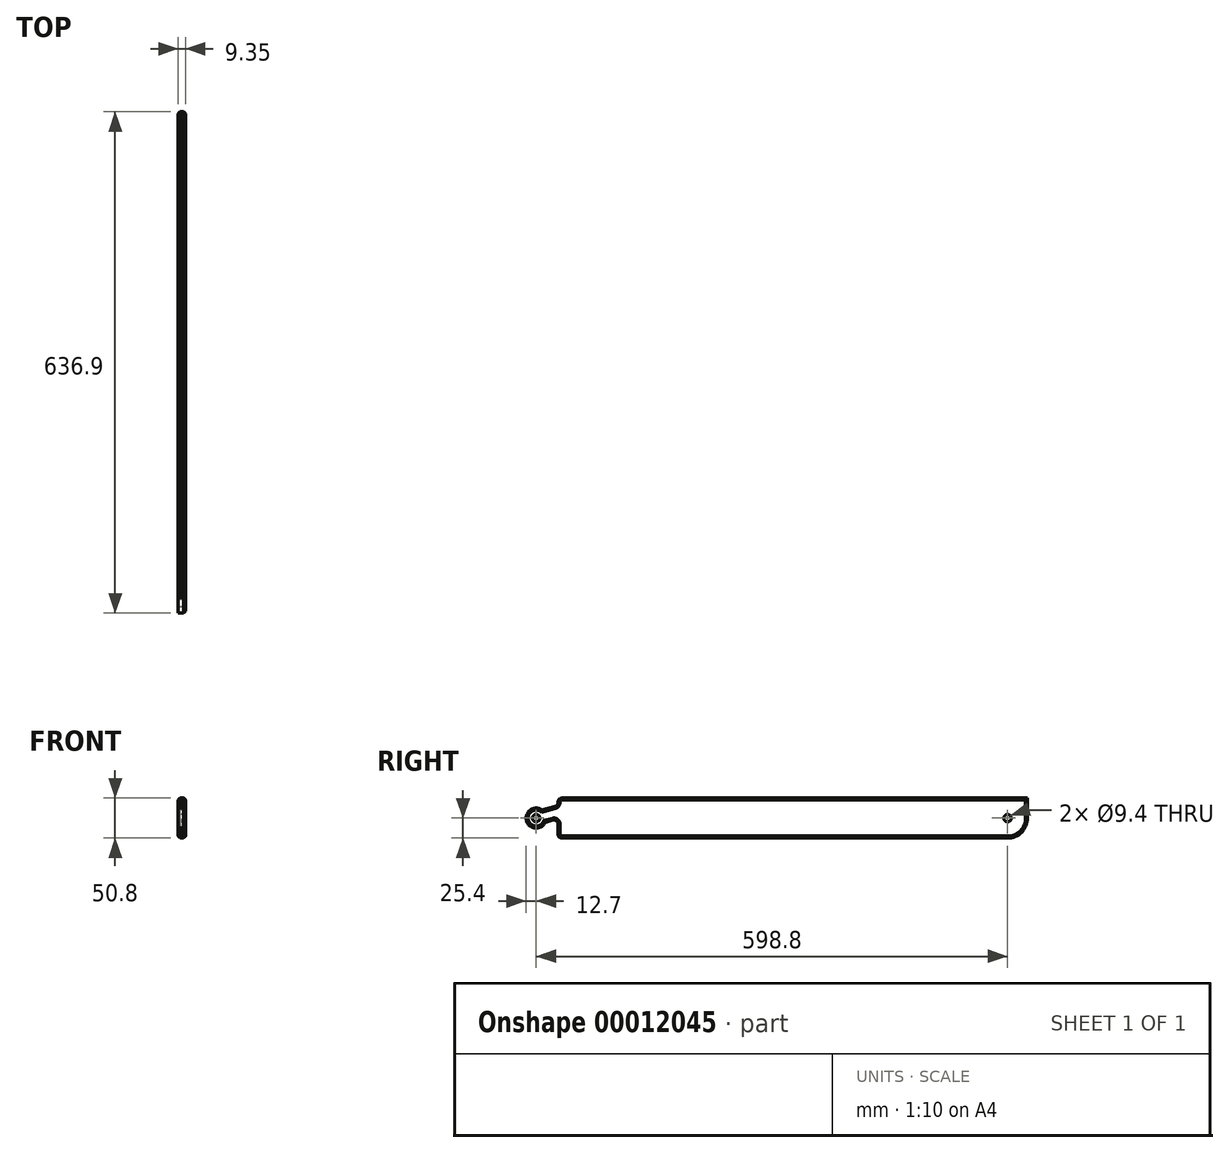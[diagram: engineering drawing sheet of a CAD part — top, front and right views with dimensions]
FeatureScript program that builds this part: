
annotation { "Feature Type Name" : "Feature", "Feature Type Description" : "" }
export const myFeature = defineFeature(function(context is Context, id is Id, definition is map)
    precondition{}
    {
        {
            var Q0;
            Q0=qCreatedBy(makeId("Right.planeOp"),FACE);
            var sketch = newSketch(context, id + "F0", { "sketchPlane" : qUnion([Q0])});
            skArc(sketch, "E0", {"start": v(7.46, 10.28) * mm, "mid": v(-12.27, -3.29) * mm, "end": v(11.6, -5.17) * mm});
            skLineSegment(sketch, "E1.0", {"start": v(11.6, -5.17) * mm, "end": v(21.4, -2.55) * mm});
            skLineSegment(sketch, "E2.0", {"start": v(7.46, 10.28) * mm, "end": v(24, 14.71) * mm});
            skLineSegment(sketch, "E3", {"start": v(27.7, 20.4) * mm, "end": v(27.7, 19.54) * mm});
            skLineSegment(sketch, "E4.0", {"start": v(32.7, -25.4) * mm, "end": v(598.8, -25.4) * mm});
            skLineSegment(sketch, "E5.0", {"start": v(32.7, 25.4) * mm, "end": v(624.2, 25.4) * mm});
            skPoint(sketch, "E6.visualSharp", {"position": v(27.7, 25.4) * mm});
            skArc(sketch, "E6.filletArc", {"start": v(32.7, 25.4) * mm, "mid": v(29.16, 23.94) * mm, "end": v(27.7, 20.4) * mm});
            skPoint(sketch, "E7.visualSharp", {"position": v(27.7, -25.4) * mm});
            skArc(sketch, "E7.filletArc", {"start": v(27.7, -20.4) * mm, "mid": v(29.16, -23.94) * mm, "end": v(32.7, -25.4) * mm});
            skLineSegment(sketch, "E8.trimOffspring", {"start": v(27.7, -7.38) * mm, "end": v(27.7, -20.4) * mm});
            skPoint(sketch, "E9.visualSharp", {"position": v(27.7, 15.7) * mm});
            skArc(sketch, "E9.filletArc", {"start": v(24, 14.71) * mm, "mid": v(26.67, 16.5) * mm, "end": v(27.7, 19.54) * mm});
            skPoint(sketch, "E10.visualSharp", {"position": v(27.7, -0.86) * mm});
            skArc(sketch, "E10.filletArc", {"start": v(27.7, -7.38) * mm, "mid": v(25.74, -3.4) * mm, "end": v(21.4, -2.55) * mm});
            skCircle(sketch, "E11", {"center": v(0, 0) * mm, "radius": 4.7 * mm});
            skLineSegment(sketch, "E12", {"start": v(624.2, 25.4) * mm, "end": v(624.2, 0) * mm});
            skCircle(sketch, "E13", {"center": v(598.8, 0) * mm, "radius": 4.7 * mm});
            skPoint(sketch, "E14.visualSharp", {"position": v(624.2, -25.4) * mm});
            skArc(sketch, "E14.filletArc", {"start": v(598.8, -25.4) * mm, "mid": v(616.76, -17.96) * mm, "end": v(624.2, 0) * mm});
            skSolve(sketch);
        }
        {
            var Q0;
            Q0=makeQuery(id+"F0.imprint","IMPRINT",FACE,{"disambiguationData":[TD([[makeQuery(id+"F0.imprint","IMPRINT",EDGE,{"derivedFrom":sQuery(id+"F0.wireOp",EDGE,"E0")}),1.0]])]});
            extrude(context, id + "F1", {"entities" : qUnion([Q0]), "depth" : 9.35 * mm});
        }
        {
            var Q0;
            Q0=makeQuery(id+"F1.opExtrude","CAP_EDGE",EDGE,{"disambiguationData":[OSD([sQuery(id+"F0.wireOp",EDGE,"E2.0")])],"isStart":false});
            var Q1;
            Q1=makeQuery(id+"F1.opExtrude","CAP_EDGE",EDGE,{"disambiguationData":[OSD([sQuery(id+"F0.wireOp",EDGE,"E2.0")])],"isStart":true});
            var Q2;
            Q2=makeQuery(id+"F1.opExtrude","CAP_EDGE",EDGE,{"disambiguationData":[OSD([sQuery(id+"F0.wireOp",EDGE,"E1.0")])],"isStart":false});
            var Q3;
            Q3=makeQuery(id+"F1.opExtrude","CAP_EDGE",EDGE,{"disambiguationData":[OSD([sQuery(id+"F0.wireOp",EDGE,"E1.0")])],"isStart":true});
            var Q4;
            Q4=makeQuery(id+"F1.opExtrude","CAP_EDGE",EDGE,{"disambiguationData":[OSD([sQuery(id+"F0.wireOp",EDGE,"E0")])],"isStart":false});
            chamfer(context, id + "F2", {"entities" : qUnion([Q0, Q1, Q2, Q3, Q4]), "width" : 2.5 * mm, "tangentPropagation" : true});
        }
    });
